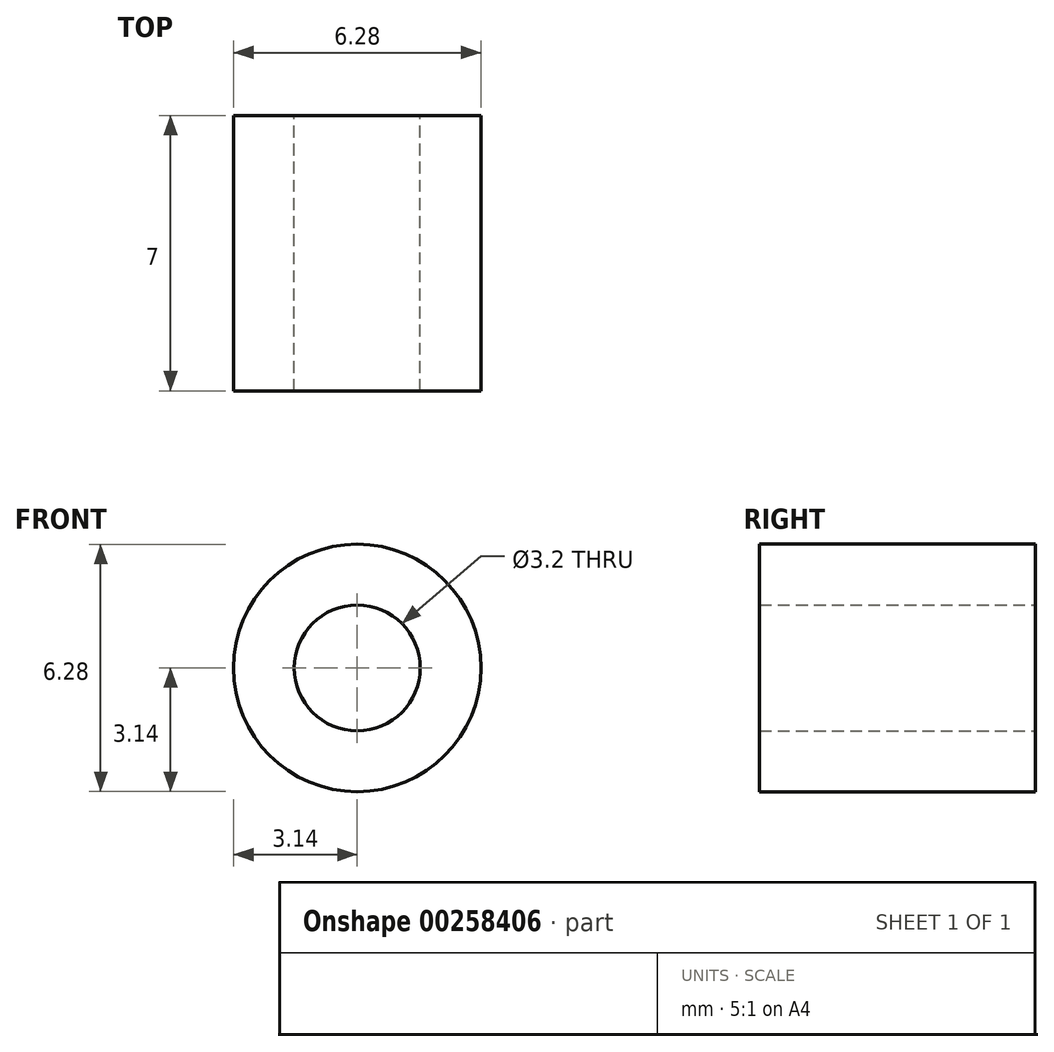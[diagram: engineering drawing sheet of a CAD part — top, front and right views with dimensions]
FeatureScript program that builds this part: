
annotation { "Feature Type Name" : "Feature", "Feature Type Description" : "" }
export const myFeature = defineFeature(function(context is Context, id is Id, definition is map)
    precondition{}
    {
        {
            var Q0;
            Q0=qCreatedBy(makeId("Front.planeOp"),FACE);
            var sketch = newSketch(context, id + "F0", { "sketchPlane" : qUnion([Q0])});
            skCircle(sketch, "E0", {"center": v(0, 0) * mm, "radius": 3.14 * mm});
            skCircle(sketch, "E1", {"center": v(0, 0) * mm, "radius": 1.6 * mm});
            skSolve(sketch);
        }
        {
            var Q0;
            Q0=makeQuery(id+"F0.imprint","IMPRINT",FACE,{"disambiguationData":[TD([[makeQuery(id+"F0.imprint","IMPRINT",EDGE,{"derivedFrom":sQuery(id+"F0.wireOp",EDGE,"E0")}),1.0]])]});
            extrude(context, id + "F1", {"entities" : qUnion([Q0]), "depth" : 7 * mm});
        }
    });
